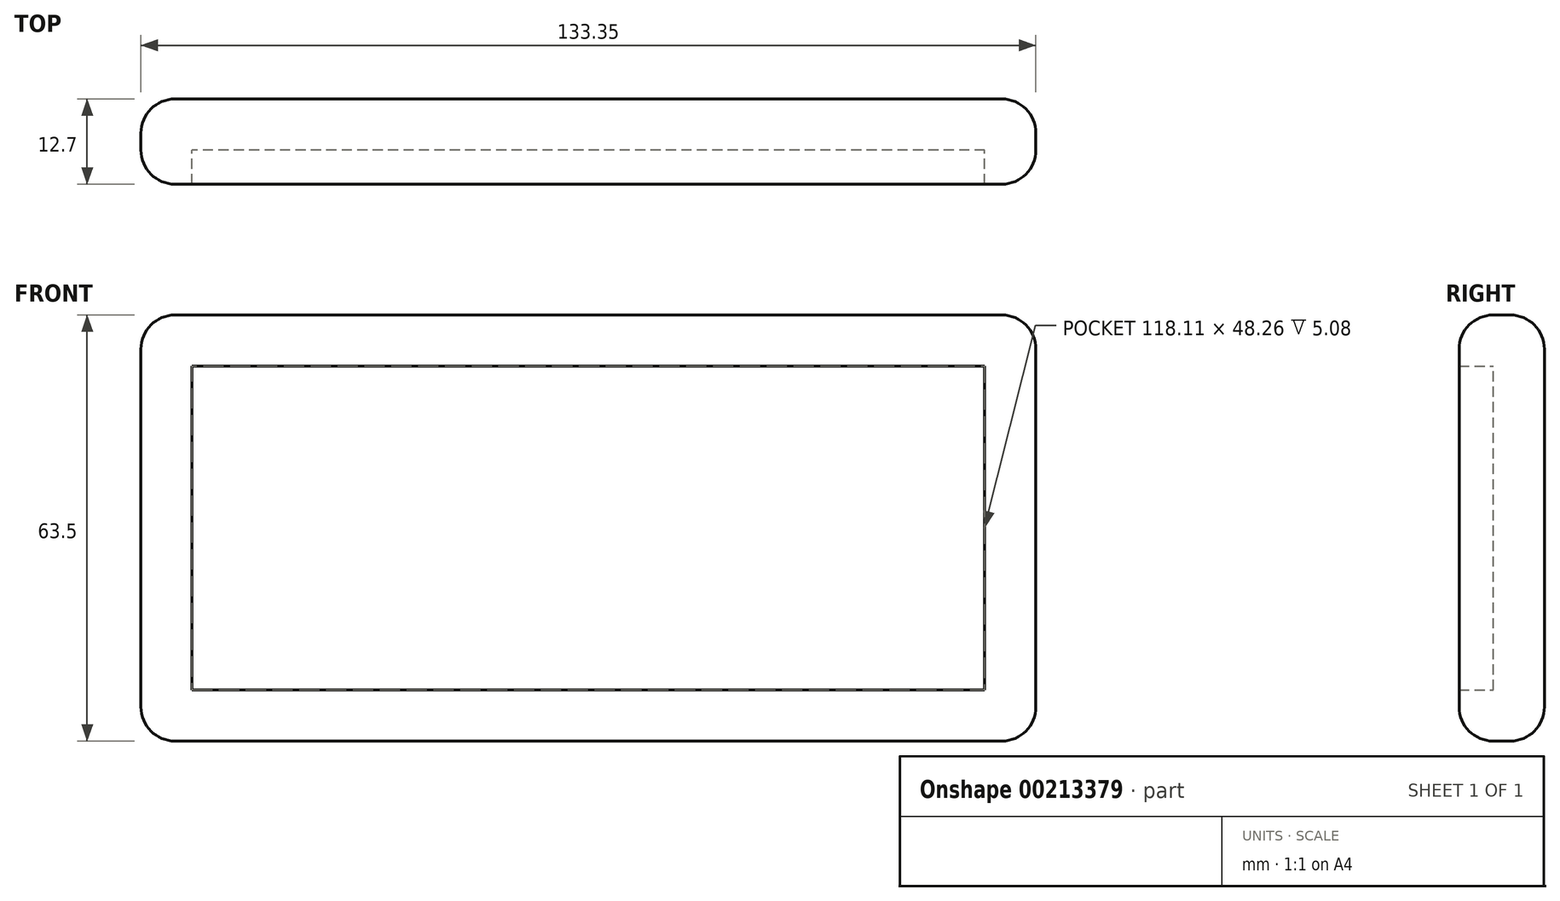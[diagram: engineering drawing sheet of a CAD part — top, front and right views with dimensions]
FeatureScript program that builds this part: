
annotation { "Feature Type Name" : "Feature", "Feature Type Description" : "" }
export const myFeature = defineFeature(function(context is Context, id is Id, definition is map)
    precondition{}
    {
        {
            var Q0;
            Q0=qCreatedBy(makeId("Front.planeOp"),FACE);
            var sketch = newSketch(context, id + "F0", { "sketchPlane" : qUnion([Q0])});
            skLineSegment(sketch, "E0.bottom", {"start": v(-72.02, 27.37) * mm, "end": v(61.33, 27.37) * mm});
            skLineSegment(sketch, "E0.top", {"start": v(-72.02, -36.13) * mm, "end": v(61.33, -36.13) * mm});
            skLineSegment(sketch, "E0.left", {"start": v(-72.02, 27.37) * mm, "end": v(-72.02, -36.13) * mm});
            skLineSegment(sketch, "E0.right", {"start": v(61.33, 27.37) * mm, "end": v(61.33, -36.13) * mm});
            skSolve(sketch);
        }
        {
            var Q0;
            Q0=makeQuery(id+"F0.imprint","IMPRINT",FACE,{"disambiguationData":[TD([[makeQuery(id+"F0.imprint","IMPRINT",EDGE,{"derivedFrom":sQuery(id+"F0.wireOp",EDGE,"E0.bottom")}),-1.0]])]});
            extrude(context, id + "F1", {"entities" : qUnion([Q0]), "endBound" : BoundingType.SYMMETRIC, "depth" : 12.7 * mm});
        }
        {
            var Q0;
            Q0=makeQuery(id+"F1.opExtrude","SWEPT_FACE",FACE,{"disambiguationData":[OSD([sQuery(id+"F0.wireOp",EDGE,"E0.left")])]});
            var Q1;
            Q1=makeQuery(id+"F1.opExtrude","SWEPT_FACE",FACE,{"disambiguationData":[OSD([sQuery(id+"F0.wireOp",EDGE,"E0.bottom")])]});
            var Q2;
            Q2=makeQuery(id+"F1.opExtrude","SWEPT_FACE",FACE,{"disambiguationData":[OSD([sQuery(id+"F0.wireOp",EDGE,"E0.right")])]});
            var Q3;
            Q3=makeQuery(id+"F1.opExtrude","SWEPT_FACE",FACE,{"disambiguationData":[OSD([sQuery(id+"F0.wireOp",EDGE,"E0.top")])]});
            fillet(context, id + "F2", {"entities" : qUnion([Q0, Q1, Q2, Q3]), "radius" : 5.08 * mm, "tangentPropagation" : true, "allowEdgeOverflow" : false});
        }
        {
            var Q0;
            Q0=makeQuery(id+"F1.opExtrude","CAP_FACE",FACE,{"disambiguationData":[OSD([sQuery(id+"F0.wireOp",EDGE,"E0.bottom"),sQuery(id+"F0.wireOp",EDGE,"E0.top"),sQuery(id+"F0.wireOp",EDGE,"E0.left"),sQuery(id+"F0.wireOp",EDGE,"E0.right")])],"isStart":false});
            shell(context, id + "F3", {"entities" : qUnion([Q0]), "thickness" : 7.62 * mm});
        }
    });
